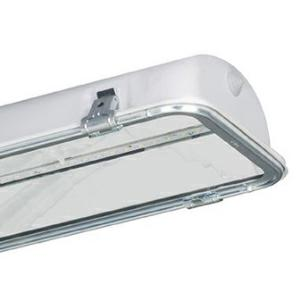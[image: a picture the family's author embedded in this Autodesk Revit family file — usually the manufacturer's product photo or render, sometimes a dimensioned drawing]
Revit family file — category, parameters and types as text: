
# Revit family: 3f_filippi_-_beta_i3f_76_vt_ampio_3f_filippi_-_55072_-_i3f_led_762x30w_ampio_vt_l1565
name_source: partatom
category: Lighting Fixtures
units: mm (PartAtom-declared; Revit-internal decimal feet)

## family parameters
Cut with Voids When Loaded = No
Host = Face
Light Source = No
Part Type = Normal
Room Calculation Point = No
Round Connector Dimension = Use Diameter
Shared = No

## types (1)
- 3F Filippi - Beta i3F 76 VT Ampio (1 x LED, 9769 lm, 66 W, 4000 K)
    Apparent Load = 66 VA
    Approval mark = ENEC
    CIE Flux Codes = 52 86 99 100 100
    Color Rendering = 80
    Color Temperature = 4000 K
    Control Gear = Electronic ballast
    Default Elevation = 1800 mm
    Description = ILLUMINOTECHNICAL
Luminous efficiency 100% (DLOR 100%, ULOR 0%).
Initial luminous flux of the luminaire 9769 lm.
Wide symmetric distribution.
Installation Interdistance Transv.D = 1.47 x hu - Long.D = 1.27 x hu.
Tabular UGR (CIE 117 - 4H-8H; S=0.25H; 70/50/20): RUG 21.3 - 24.6.
Beam angle: 101° - 108°.
Luminous efficacy 148 lm/W.
Lifetime (L93/B10): 30000 h. (tq+25°C)
Lifetime (L90/B10): 50000 h. (tq+25°C)
Lifetime (L85/B10): 80000 h. (tq+25°C)
Lifetime (L80/B10): 100000 h. (tq+25°C)
Lifetime (L85/B10): 50000 h. (tq+35°C)
Sudden decreased luminous flux after 50000 hours: 0% (C0).
Photobiological safety in compliance with IEC/TR 62778: RG0 risk exempt, (IEC 62471).
In compliance with IEC/EN 62722-2-1 - IEC/EN 62717 standards.

SOURCE
2 linear LED modules 30W/840.
Energy efficiency class (UE 2019/2020 - UE 2019/2015): D.
CIE 13.3 Colour rendering index: CRI >80 (R9 <50%).
IES TM-30 Fidelity Index: Rf = 84 Rg = 95.
CCT nominal colour temperature 4000 K.
Colour initial tolerance (MacAdam): SDCM 3.

MECHANICAL
Single-piece housing in pressed steel, powder-coated in white epoxy-polyester.
Transparent glass, non-combustible, tempered, mounted and locked to the single-piece galvanised steel perimetrical frame, sealing gasket, hinged opening by means of galvanised steel clips.
Wide flow recuperator, oversized, in specular aluminium with superficial titanium-magnesium treatment, non-iridescent.
Gear-tray unit in hot-galvanised steel, painted in white polyester, fixed to the housing by means of "Ribloc" rapid devices in galvanised steel, hinged opening.
Luminaire with limited surface temperature. - D - (EN 60598-2-24)
Dimensions: 1565x235 mm, height 105 mm. Weight 9.82 kg.
IP65 protection degree.
Mechanical strength to impacts IK09 (10 joule).
Glow-wire test resistance 960°C.

ELECTRICAL
Halogen Free electronic wiring 230V-50/60Hz, power factor 0.97, THD <25%, constant output current, SELV, class I, 1 driver.
Power of the luminaire 66 W.
CE - IEC 60598-1 - EN 60598-1.
SAFE FLICKER: PstLM=<1 and SVM=<0.4 (IEC TR 61547-1 and IEC TR 63158), to ensure a more comfortable and safe light.
Luminaire compliant with EN 60598-2-22 for power supply from a centralised emergency system CPSS (Central Power Supply System), not incorporated in the luminaire - high risk areas excluded. The default power and flux are 100% in AC and 100% in DC.
Ambient temperature from -20°C to +35°C.
Temperature class T6 max 85°C.
Relative humidity UR: <85%.

INSTALLATION
Ceiling / Suspended / Wall.
All accessories dedicated to this product are available on the Catalog and on our website www.3F-Filippi.com.

APPLICATIONS
In industrial environments, stores and dry, dusty indoor environments, subject to occasional water splashes.

WARNING
Fixture not suitable for cold stores with an ambient temperature <0°C and/or relative humidity >85%.
Luminaire designed for disposal/recycling at end-of-life.
Replaceable (LED only) light source by a professional. Replaceable control gear by a professional.
    Height = 105 mm
    Lamp = 1 x LED
    Lamp Light Flux = 9769 lm
    Lamp Power = 66 W
    Lamp count = 1
    Length = 1565 mm
    Lifetime = 50000 h
    Luminous efficacy = 148 lm/W
    Manufacturer = 3F Filippi
    ModVariant = No
    Model = 3F Filippi - 55072 - i3F LED 762x30W AMPIO VT L1565
    Mounting Place = Ceiling
    Mounting Type = Pendant
    Number of Poles = 1
    OnlyDefault = Yes
    Power Factor = 1
    Product Name = 3F Filippi - Beta i3F 76 VT Ampio
    Product group = pendant luminaire
    ProductGroupID = 9
    Protection Class = Protection class I
    Protection Degree = IP 65
    RLX_Detail_Level = 1
    RLX_Emergency_Light_Flux = 0 lm
    RLX_Emergency_Type = 0
    RLX_Emergency_Type_DB = No
    RlxData = <blob elided: 70193 chars, md5=460621f0>
    Socket = socket
    Standby Power = 0 W
    System Light Flux = 9769 lm
    System Power = 66 W
    Type Comments = Product without accessories
    Type Image = 3ffilippi_55072.jpg
    URL = http://relux.com
    VarID = ---
    Voltage = 0 V
    Weight = 0.00 kg
    Width = 235 mm

## geometry (parser evidence)
native form markers: Blend x4, Sweep x9
no freeform markers — native parametric forms only
